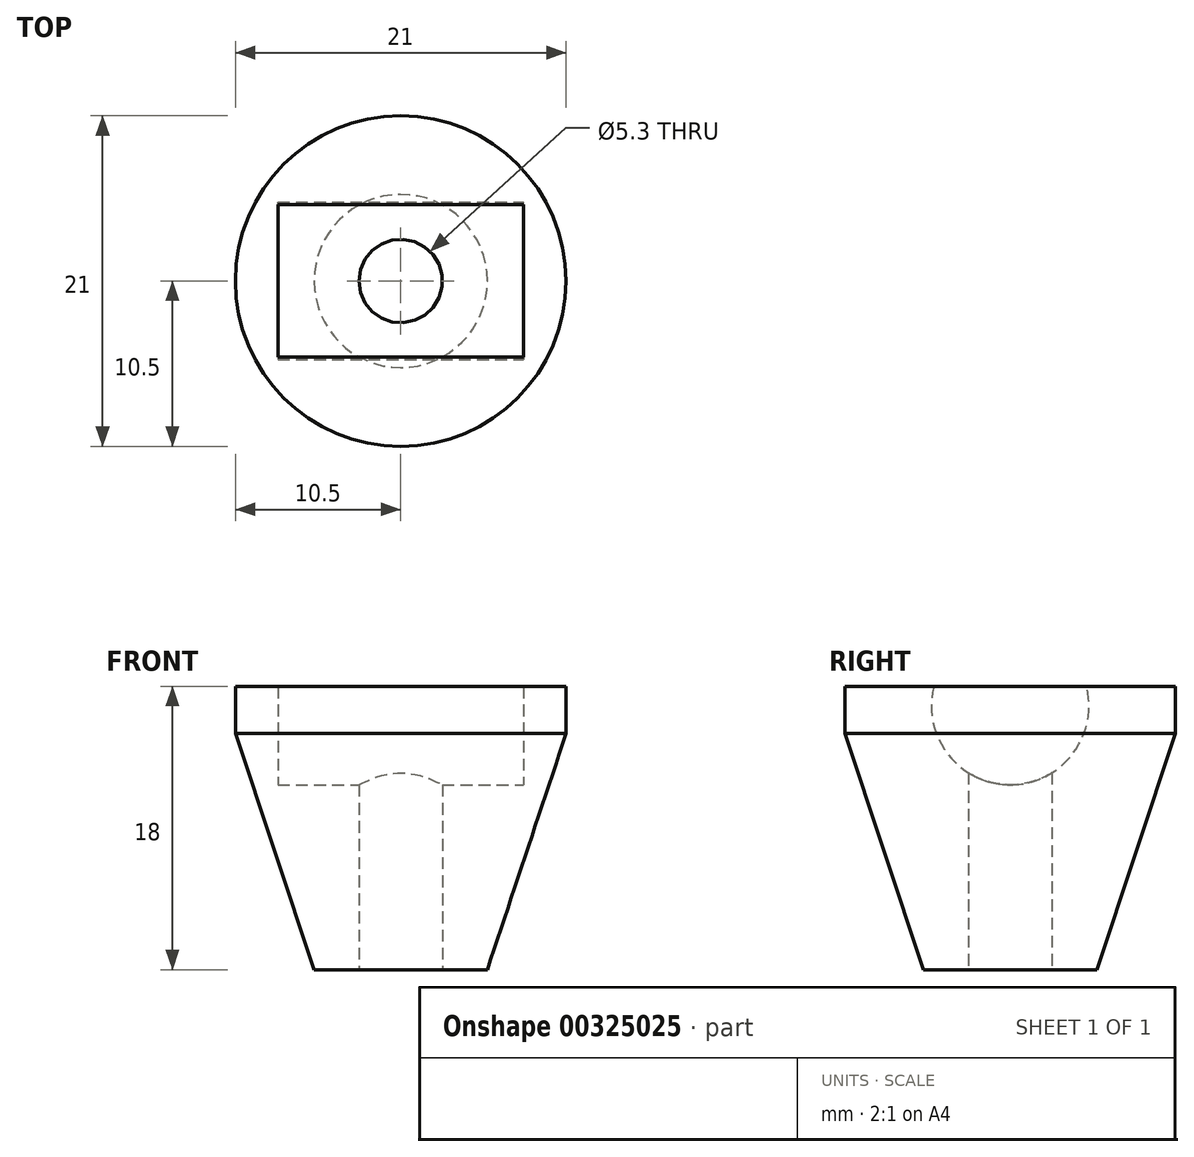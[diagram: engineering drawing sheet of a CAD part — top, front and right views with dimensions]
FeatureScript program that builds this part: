
annotation { "Feature Type Name" : "Feature", "Feature Type Description" : "" }
export const myFeature = defineFeature(function(context is Context, id is Id, definition is map)
    precondition{}
    {
        {
            var Q0;
            Q0=qCreatedBy(makeId("Top.planeOp"),FACE);
            var sketch = newSketch(context, id + "F0", { "sketchPlane" : qUnion([Q0])});
            skCircle(sketch, "E0", {"center": v(0, 0) * mm, "radius": 10.5 * mm});
            skCircle(sketch, "E1", {"center": v(0, 0) * mm, "radius": 2.65 * mm});
            skSolve(sketch);
        }
        {
            var Q0;
            Q0=makeQuery(id+"F0.imprint","IMPRINT",FACE,{"disambiguationData":[TD([[makeQuery(id+"F0.imprint","IMPRINT",EDGE,{"derivedFrom":sQuery(id+"F0.wireOp",EDGE,"E0")}),1.0]])]});
            extrude(context, id + "F1", {"entities" : qUnion([Q0]), "depth" : 18 * mm});
        }
        {
            var Q0;
            Q0=qCreatedBy(makeId("Right.planeOp"),FACE);
            var sketch = newSketch(context, id + "F2", { "sketchPlane" : qUnion([Q0])});
            skCircle(sketch, "E2", {"center": v(0, 16.75) * mm, "radius": 5 * mm});
            skSolve(sketch);
        }
        {
            var Q0;
            Q0=makeQuery(id+"F2.imprint","IMPRINT",FACE,{"disambiguationData":[TD([[makeQuery(id+"F2.imprint","IMPRINT",EDGE,{"derivedFrom":sQuery(id+"F2.wireOp",EDGE,"E2")}),1.0]])]});
            extrude(context, id + "F3", {"entities" : qUnion([Q0]), "operationType" : NewBodyOperationType.REMOVE, "oppositeDirection" : true, "depth" : 7.8 * mm, "hasSecondDirection" : true, "secondDirectionOppositeDirection" : false, "secondDirectionDepth" : 7.8 * mm});
        }
        {
            var Q0;
            Q0=makeQuery(id+"F1.opExtrude","CAP_EDGE",EDGE,{"disambiguationData":[OSD([sQuery(id+"F0.wireOp",EDGE,"E0")])],"isStart":true});
            chamfer(context, id + "F4", {"entities" : qUnion([Q0]), "chamferType" : ChamferType.TWO_OFFSETS, "width1" : 15 * mm, "oppositeDirection" : false, "width2" : 5 * mm, "tangentPropagation" : true});
        }
    });
